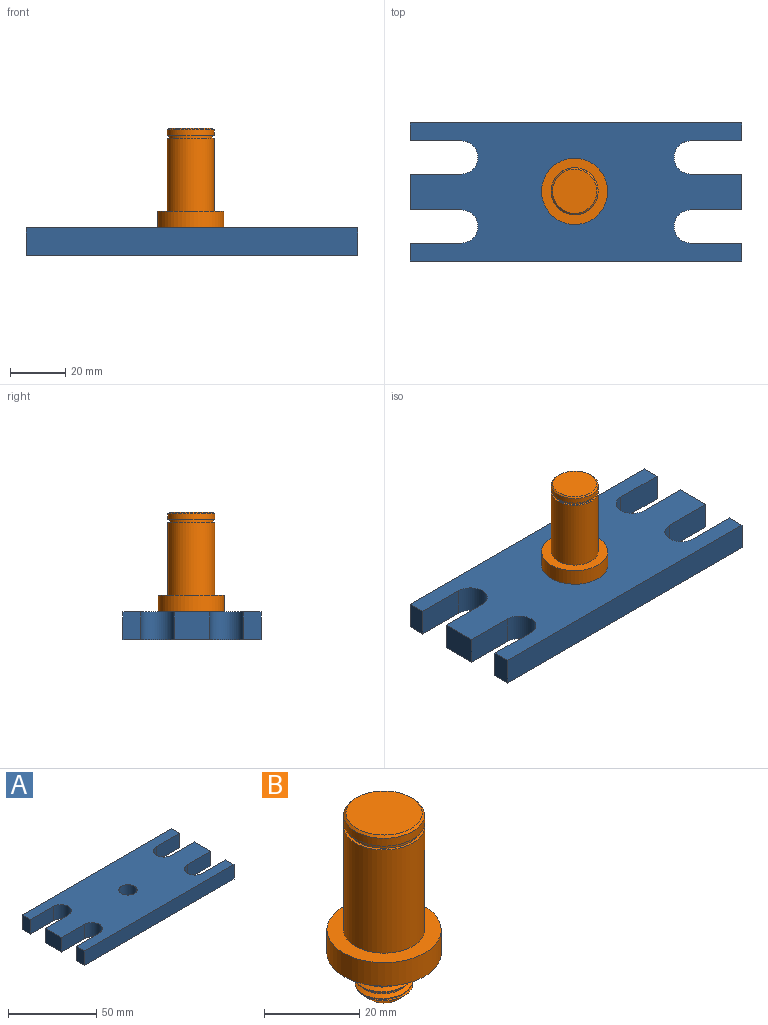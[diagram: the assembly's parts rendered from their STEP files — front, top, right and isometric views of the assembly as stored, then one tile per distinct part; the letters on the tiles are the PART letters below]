
ASSEMBLY  parts=2 mates=1
PART A: 24 faces, bbox 120x50x10 mm
  f0: plane 18.5x10mm, normal (0,1,0), area 185mm2, adj f1,f19,f20,f21
  f1: plane 13x10mm, normal (-1,0,0), area 130mm2, adj f0,f2,f20,f21
  f2: plane 18.5x10mm, normal (0,-1,0), area 185mm2, adj f1,f3,f20,f21
  f3: cylinder r=6mm len=12mm, axis (0,0,-1), area 188.5mm2, adj f2,f4,f20,f21
  f4: plane 18.5x10mm, normal (0,1,0), area 185mm2, adj f3,f5,f20,f21
  f5: plane 10x6.5mm, normal (-1,0,0), area 65mm2, adj f4,f6,f20,f21
  f6: plane 120x10mm, normal (0,-1,0), area 1200mm2, adj f5,f7,f20,f21
  f7: plane 10x6.5mm, normal (1,0,0), area 65mm2, adj f6,f8,f20,f21
  f8: plane 18.5x10mm, normal (0,1,0), area 185mm2, adj f7,f9,f20,f21
  f9: cylinder r=6mm len=12mm, axis (0,0,-1), area 188.5mm2, adj f8,f10,f20,f21
  f10: plane 18.5x10mm, normal (0,-1,0), area 185mm2, adj f9,f11,f20,f21
  f11: plane 13x10mm, normal (1,0,0), area 130mm2, adj f10,f12,f20,f21
  f12: plane 18.5x10mm, normal (0,1,0), area 185mm2, adj f11,f13,f20,f21
  f13: cylinder r=6mm len=12mm, axis (0,0,-1), area 188.5mm2, adj f12,f14,f20,f21
  f14: plane 18.5x10mm, normal (0,-1,0), area 185mm2, adj f13,f15,f20,f21
  f15: plane 10x6.5mm, normal (1,0,0), area 65mm2, adj f14,f16,f20,f21
  f16: plane 120x10mm, normal (0,1,0), area 1200mm2, adj f15,f17,f20,f21
  f17: plane 10x6.5mm, normal (-1,0,0), area 65mm2, adj f16,f18,f20,f21
  f18: plane 18.5x10mm, normal (0,-1,0), area 185mm2, adj f17,f19,f20,f21
  f19: cylinder r=6mm len=12mm, axis (0,0,-1), area 188.5mm2, adj f0,f18,f20,f21
  f20: plane 120x50mm, normal (0,0,1), area 4802.5mm2, adj f0,f1,f2,f3,f4,f5,f6,f7
  f21: plane 120x50mm, normal (0,0,-1), area 4725.2mm2, adj f0,f1,f2,f3,f4,f5,f6,f7
  f22: cylinder r=5.15mm len=10.3mm, axis (0,0,1), area 258.9mm2, adj f20,f23
  f23: cone r=5.15mm half-angle=45deg, axis (0,0,-1), area 109.3mm2, adj f21,f22
PART B: 17 faces, bbox 24.5x24.5x46.5 mm
  f0: cylinder r=12mm len=24mm, axis (0,0,-1), area 452.4mm2, adj f1,f2
  f1: plane 24x24mm, normal (0,0,1), area 225.4mm2, adj f0,f8
  f2: plane 24.49x24.49mm, normal (0,0,-1), area 358.6mm2, adj f0,f10,f13,f14,f15
  f3: plane 16x16mm, normal (0,0,1), area 201.1mm2, adj f9
  f4: cylinder r=8.5mm len=17mm, axis (0,0,-1), area 106.8mm2, adj f5,f9
  f5: plane 17x17mm, normal (0,0,-1), area 33.4mm2, adj f4,f6
  f6: cylinder r=7.85mm len=15.7mm, axis (0,0,-1), area 49.3mm2, adj f5,f7
  f7: plane 17x17mm, normal (0,0,1), area 33.4mm2, adj f6,f8
  f8: cylinder r=8.5mm len=26.5mm, axis (0,0,-1), area 1415.3mm2, adj f1,f7
  f9: cone r=8.5mm half-angle=45deg, axis (0,0,-1), area 36.7mm2, adj f3,f4
  f10: cylinder r=6mm len=12mm, axis (0,0,1), area 38.5mm2, adj f2,f12,f14,f15
  f11: plane 8x8mm, normal (0,0,-1), area 50.3mm2, adj f12
  f12: cone r=4mm half-angle=45deg, axis (0,0,1), area 88.9mm2, adj f10,f11,f16
  f13: bspline ~11.67x10.11mm, area 70.3mm2, adj f2,f14,f15,f16
  f14: bspline ~13.86x12mm, area 173.7mm2, adj f2,f10,f13,f16
  f15: bspline ~13.86x12mm, area 173.8mm2, adj f2,f10,f13,f16
  f16: plane 12.5x12.5mm, normal (0,0,1), area 19.3mm2, adj f12,f13,f14,f15
PLACE A at identity
PLACE B t=(-0.49,0.2,10)mm
MATE fastened B.f2 <-> A.f22  axis (0,0,-1) through (0,0,10)mm
